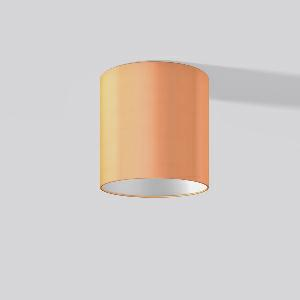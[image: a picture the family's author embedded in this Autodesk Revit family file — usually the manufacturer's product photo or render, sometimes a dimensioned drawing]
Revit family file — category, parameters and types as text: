
# Revit family: toledo_flatliner_901630_002_1_76_9910
name_source: partatom
category: Lighting Fixtures
units: mm (PartAtom-declared; Revit-internal decimal feet)

## family parameters
Cut with Voids When Loaded = No
Host = Face
Light Source = No
Part Type = Normal
Room Calculation Point = No
Round Connector Dimension = Use Diameter
Shared = No

## types (1)
- 982300.002 (1 x LED Modul 840, 660 lm, 4000)
    Apparent Load = 8 VA
    CIE Flux Codes = 56 78 92 81 100
    Color Rendering = 80
    Color Temperature = 4000
    Default Elevation = 1800 mm
    Description = Series: TOLEDO FLATLINER
Decorative ceiling luminaire for interior decoration. Base luminaire prepared for the installation of fabric lampshade. Cylinder housing sheet steel, powder-coated. Housing: die cast aluminium and sheet steel, powder-coated. Bezel ring: die-cast aluminium, powder-coated. Lightguide and diffuser made of non-yellowing plastic (PMMA) opal matt. Modular design: With the basic luminaire, a square or cylindrical fabric lampshade must always be ordered separately. Fabric lampshades can be fitted to the basic luminaire without tools. Order satin finish diffuser as separate accessory. 
Colour: white
Diameter: 202 mm
Height: 65 mm
Lamp: LED
Socket: without socket
Colour temperature: 4000K
Colour rendering index (CRI): 80
System power: 7.7 W
Rated luminous flux: 660 lm
Luminous efficiency: 86 lm/W
Control gear: Converter, dimmable, DALI
Protection class: II
Type of protection: IP 40
    Height = 65 mm
    Lamp = 1 x LED Modul 840
    Lamp Light Flux = 660 lm
    Lamp count = 1
    Length = 202 mm
    Lifetime = 50000 h
    Luminous efficacy = 86 lm/W
    Manufacturer = RZB
    ModVariant = No
    Model = 901630.002.1.76
    Mounting Place = Ceiling
    Mounting Type = Surface mounted
    Number of Poles = 1
    OnlyDefault = Yes
    Power Factor = 1
    Product Name = TOLEDO FLATLINER
    Product group = Surface mounted ceiling Fabric lampshade luminaires
    ProductGroupID = 313
    Protection Class = Protection class II
    Protection Degree = IP 40
    RLX_Detail_Level = 1
    RLX_Emergency_Light_Flux = 0 lm
    RLX_Emergency_Type = 0
    RLX_Emergency_Type_DB = No
    RlxData = <blob elided: 62585 chars, md5=7e546479>
    Socket = socket
    Standby Power = 0 W
    System Light Flux = 660 lm
    System Power = 8 W
    Type Image = toledo_flatliner_anbau_rund_orange_odeckel.jpg
    URL = http://relux.com
    VarID = 982300_002_5a54
    Voltage = 230 V
    Voltage Range = 220-240 V
    Weight = 0.00 kg
    Width = 0 mm  [stored 0 ft]

note: [stored X ft] marks values corroborated as IEEE doubles in the binary element streams (Revit-internal decimal feet)

## geometry (parser evidence)
native form markers: Blend x4, Sweep x13
no freeform markers — native parametric forms only
